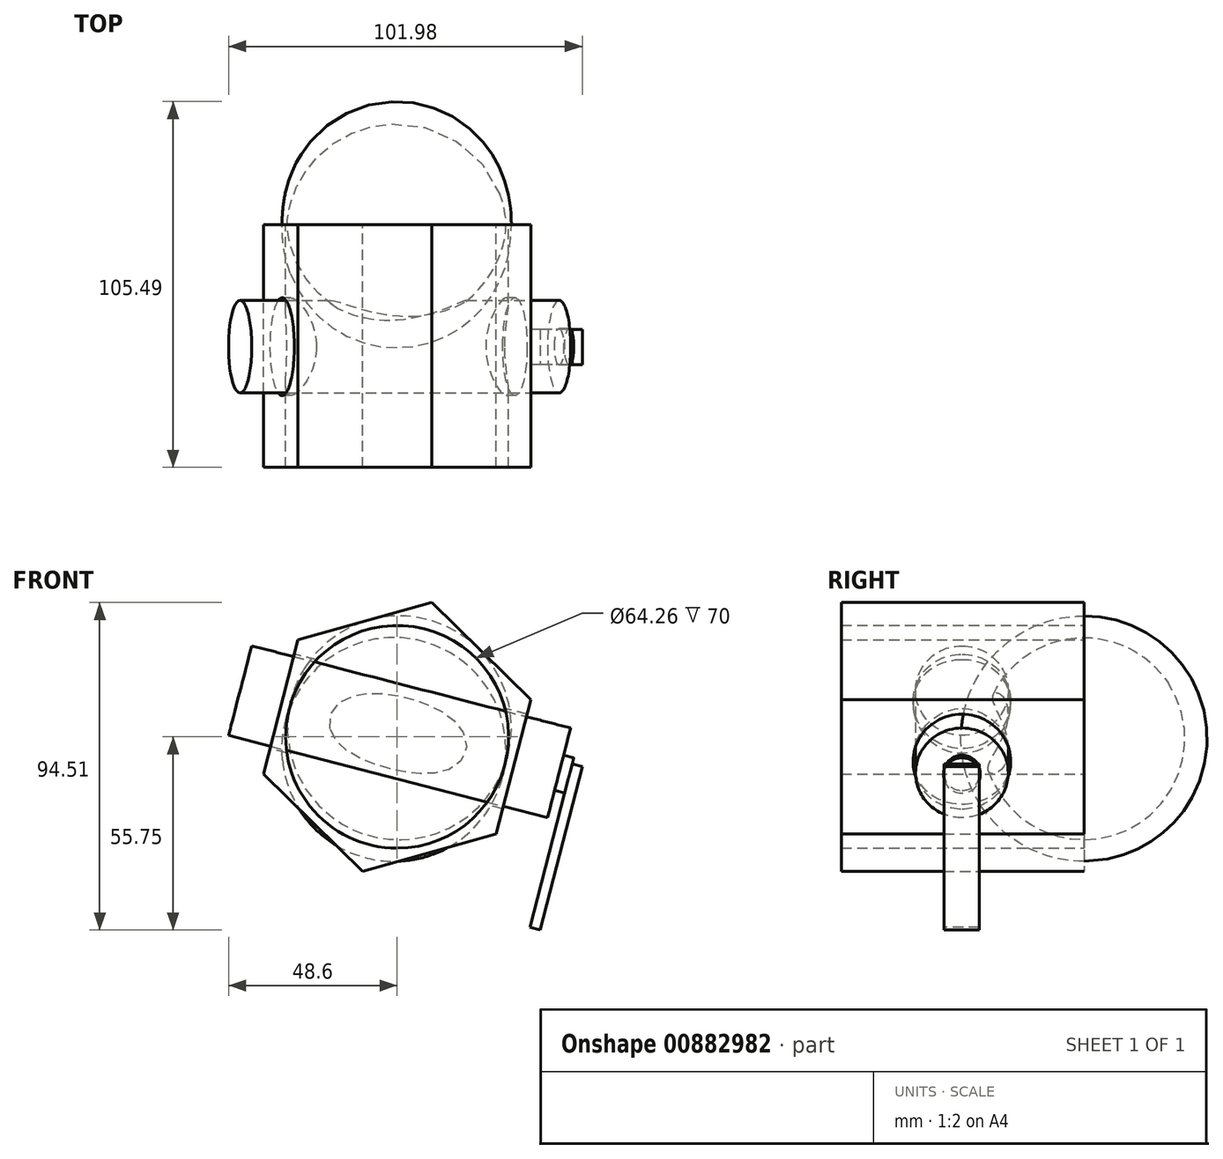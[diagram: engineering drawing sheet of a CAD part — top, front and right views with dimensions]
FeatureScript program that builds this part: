
annotation { "Feature Type Name" : "Feature", "Feature Type Description" : "" }
export const myFeature = defineFeature(function(context is Context, id is Id, definition is map)
    precondition{}
    {
        {
            var Q0;
            Q0=qCreatedBy(makeId("Front.planeOp"),FACE);
            var sketch = newSketch(context, id + "F0", { "sketchPlane" : qUnion([Q0])});
            skCircle(sketch, "E0.cCircle", {"center": v(0, 0) * mm, "radius": 34.66 * mm, "construction": true});
            skLineSegment(sketch, "E0.0", {"start": v(38.56, 10.72) * mm, "end": v(28.57, -28.04) * mm});
            skLineSegment(sketch, "E0.1", {"start": v(28.57, -28.04) * mm, "end": v(-10, -38.76) * mm});
            skLineSegment(sketch, "E0.2", {"start": v(-10, -38.76) * mm, "end": v(-38.56, -10.72) * mm});
            skLineSegment(sketch, "E0.3", {"start": v(-38.56, -10.72) * mm, "end": v(-28.57, 28.04) * mm});
            skLineSegment(sketch, "E0.4", {"start": v(-28.57, 28.04) * mm, "end": v(10, 38.76) * mm});
            skLineSegment(sketch, "E0.5", {"start": v(10, 38.76) * mm, "end": v(38.56, 10.72) * mm});
            skPoint(sketch, "E0.0.midPoint", {"position": v(33.56, -8.66) * mm});
            skSolve(sketch);
        }
        {
            var Q0;
            Q0=makeQuery(id+"F0.imprint","IMPRINT",FACE,{"disambiguationData":[TD([[makeQuery(id+"F0.imprint","IMPRINT",EDGE,{"derivedFrom":sQuery(id+"F0.wireOp",EDGE,"E0.0")}),-1.0]])]});
            var sketch = newSketch(context, id + "F1", { "sketchPlane" : qUnion([Q0])});
            skCircle(sketch, "E1", {"center": v(0, 0) * mm, "radius": 32.13 * mm});
            skSolve(sketch);
        }
        {
            var Q0;
            Q0=makeQuery(id+"F1.imprint","IMPRINT",FACE,{"disambiguationData":[TD([[makeQuery(id+"F1.imprint","IMPRINT",EDGE,{"derivedFrom":sQuery(id+"F1.wireOp",EDGE,"E1")}),-1.0]])]});
            extrude(context, id + "F2", {"entities" : qUnion([Q0]), "depth" : 70 * mm, "offsetDistance" : 25 * mm});
        }
        {
            var Q0;
            Q0=makeQuery(id+"F2.opExtrude","SWEPT_FACE",FACE,{"disambiguationData":[OSD([sQuery(id+"F0.wireOp",EDGE,"E0.3")])]});
            var sketch = newSketch(context, id + "F3", { "sketchPlane" : qUnion([Q0])});
            skCircle(sketch, "E2", {"center": v(35.2, 1.6) * mm, "radius": 14.1 * mm});
            skSolve(sketch);
        }
        {
            var Q0;
            Q0 = qSketchRegion(id + "F3", true);
            extrude(context, id + "F4", {"entities" : qUnion([Q0]), "operationType" : NewBodyOperationType.REMOVE, "endBound" : BoundingType.THROUGH_ALL, "oppositeDirection" : true, "depth" : 25 * mm, "offsetDistance" : 25 * mm});
        }
        {
            var Q0;
            Q0=makeQuery(id+"F2.opExtrude","SWEPT_FACE",FACE,{"disambiguationData":[OSD([sQuery(id+"F0.wireOp",EDGE,"E0.3")])]});
            var sketch = newSketch(context, id + "F5", { "sketchPlane" : qUnion([Q0])});
            skCircle(sketch, "E3", {"center": v(35.2, 1.6) * mm, "radius": 13.36 * mm});
            skSolve(sketch);
        }
        {
            var Q0;
            Q0 = qSketchRegion(id + "F5", true);
            var Q1;
            Q1=makeQuery(id+"F2.opExtrude","SWEPT_FACE",FACE,{"disambiguationData":[OSD([sQuery(id+"F1.wireOp",EDGE,"E1")])]});
            extrude(context, id + "F6", {"entities" : qUnion([Q0]), "endBound" : BoundingType.SYMMETRIC, "depth" : 25 * mm, "endBoundEntityFace" : qUnion([Q1]), "offsetDistance" : 25 * mm});
        }
        {
            var Q0;
            Q0=makeQuery(id+"F6.opExtrude","CAP_FACE",FACE,{"disambiguationData":[OSD([sQuery(id+"F5.wireOp",EDGE,"E3")])],"isStart":true});
            extrude(context, id + "F7", {"entities" : qUnion([Q0]), "operationType" : NewBodyOperationType.ADD, "depth" : 70 * mm, "offsetDistance" : 25 * mm});
        }
        {
            var Q0;
            Q0=makeQuery(id+"F7.opExtrude","CAP_FACE",FACE,{"disambiguationData":[OSD([sQuery(id+"F5.wireOp",EDGE,"E3")])],"isStart":false});
            var sketch = newSketch(context, id + "F8", { "sketchPlane" : qUnion([Q0])});
            skCircle(sketch, "E4", {"center": v(-35.2, 1.6) * mm, "radius": 5.26 * mm});
            skSolve(sketch);
        }
        {
            var Q0;
            Q0 = qSketchRegion(id + "F8", true);
            extrude(context, id + "F9", {"entities" : qUnion([Q0]), "operationType" : NewBodyOperationType.ADD, "depth" : 3 * mm, "offsetDistance" : 25 * mm});
        }
        {
            var Q0;
            Q0=makeQuery(id+"F9.opExtrude","CAP_FACE",FACE,{"disambiguationData":[OSD([sQuery(id+"F8.wireOp",EDGE,"E4")])],"isStart":false});
            var sketch = newSketch(context, id + "F10", { "sketchPlane" : qUnion([Q0])});
            skLineSegment(sketch, "E5.bottom", {"start": v(-30.2, 0) * mm, "end": v(-40.39, 0) * mm});
            skLineSegment(sketch, "E5.top", {"start": v(-30.2, -43.69) * mm, "end": v(-40.39, -43.69) * mm});
            skLineSegment(sketch, "E5.left", {"start": v(-30.2, 0) * mm, "end": v(-30.2, -43.69) * mm});
            skLineSegment(sketch, "E5.right", {"start": v(-40.39, 0) * mm, "end": v(-40.39, -43.69) * mm});
            skSolve(sketch);
        }
        {
            var Q0;
            {var subQ0=sQuery(id+"F10.wireOp",EDGE,"E5.bottom");var subQ1=makeQuery(id+"F9.opExtrude","CAP_EDGE",EDGE,{"disambiguationData":[OSD([sQuery(id+"F8.wireOp",EDGE,"E4")])],"isStart":false});var subQ3=makeQuery(id+"F10.imprint","INTERSECT",VERTEX,{"derivedFrom":[subQ1,subQ0]});Q0=makeQuery(id+"F10.imprint","IMPRINT",FACE,{"disambiguationData":[TD([[makeQuery(id+"F10.imprint","IMPRINT",EDGE,{"disambiguationData":[TD([[subQ3,1.0]])],"derivedFrom":subQ0}),1.0]])]});}
            var Q1;
            Q1=makeQuery(id+"F10.imprint","IMPRINT",FACE,{"disambiguationData":[TD([[makeQuery(id+"F10.imprint","IMPRINT",EDGE,{"derivedFrom":sQuery(id+"F10.wireOp",EDGE,"E5.top")}),-1.0]])]});
            extrude(context, id + "F11", {"entities" : qUnion([Q0, Q1]), "operationType" : NewBodyOperationType.ADD, "depth" : 3 * mm, "offsetDistance" : 25 * mm});
        }
        {
            var Q0;
            Q0=makeQuery(id+"F11.opExtrude","SWEPT_FACE",FACE,{"disambiguationData":[OSD([sQuery(id+"F10.wireOp",EDGE,"E5.bottom")])]});
            extrude(context, id + "F12", {"entities" : qUnion([Q0]), "operationType" : NewBodyOperationType.ADD, "depth" : 5 * mm, "offsetDistance" : 25 * mm});
        }
        {
            var Q0;
            Q0=makeQuery(id+"F2.opExtrude","CAP_FACE",FACE,{"disambiguationData":[OSD([sQuery(id+"F0.wireOp",EDGE,"E0.0"),sQuery(id+"F0.wireOp",EDGE,"E0.1"),sQuery(id+"F0.wireOp",EDGE,"E0.2"),sQuery(id+"F0.wireOp",EDGE,"E0.3"),sQuery(id+"F0.wireOp",EDGE,"E0.4"),sQuery(id+"F0.wireOp",EDGE,"E0.5"),sQuery(id+"F1.wireOp",EDGE,"E1")])],"isStart":true});
            var sketch = newSketch(context, id + "F13", { "sketchPlane" : qUnion([Q0])});
            skArc(sketch, "E6", {"start": v(-31.05, -8.24) * mm, "mid": v(7.12, -28.74) * mm, "end": v(31.3, 7.21) * mm});
            skLineSegment(sketch, "E7", {"start": v(31.3, 7.21) * mm, "end": v(-31.05, -8.24) * mm});
            skSolve(sketch);
        }
        {
            var Q0;
            Q0=makeQuery(id+"F13.imprint","IMPRINT",FACE,{"disambiguationData":[TD([[makeQuery(id+"F13.imprint","IMPRINT",EDGE,{"derivedFrom":sQuery(id+"F13.wireOp",EDGE,"E6")}),1.0]])]});
            var Q1;
            Q1=sQuery(id+"F13.wireOp",EDGE,"E7");
            revolve(context, id + "F14", {"operationType" : NewBodyOperationType.ADD, "surfaceOperationType" : NewSurfaceOperationType.NEW, "entities" : qUnion([Q0]), "axis" : qUnion([Q1]), "revolveType" : RevolveType.FULL});
        }
    });
